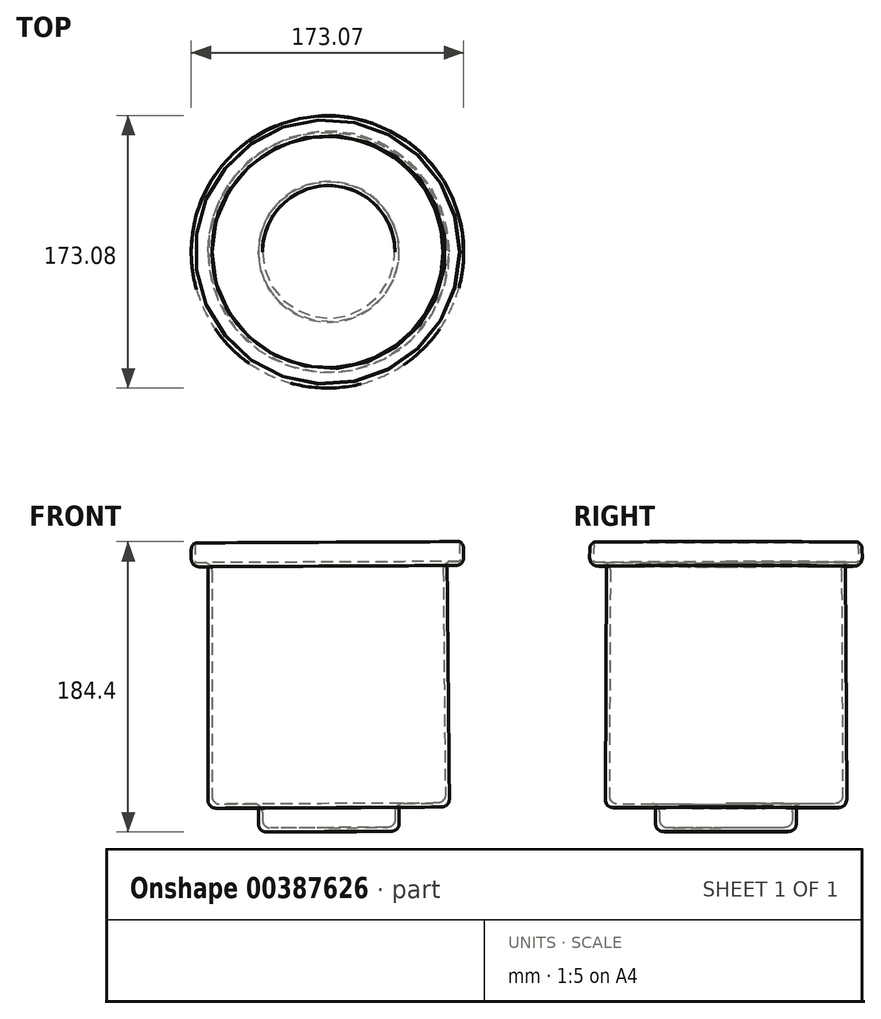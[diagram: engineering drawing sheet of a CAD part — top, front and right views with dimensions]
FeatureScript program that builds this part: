
annotation { "Feature Type Name" : "Feature", "Feature Type Description" : "" }
export const myFeature = defineFeature(function(context is Context, id is Id, definition is map)
    precondition{}
    {
        {
            var Q0;
            Q0=qCreatedBy(makeId("Front.planeOp"),FACE);
            var sketch = newSketch(context, id + "F0", { "sketchPlane" : qUnion([Q0])});
            skLineSegment(sketch, "E0.bottom", {"start": v(-75.88, 76.33) * mm, "end": v(76.77, 76.33) * mm});
            skLineSegment(sketch, "E0.top", {"start": v(-75.88, -77.03) * mm, "end": v(76.77, -77.03) * mm});
            skLineSegment(sketch, "E0.left", {"start": v(-75.88, 76.33) * mm, "end": v(-75.88, -77.03) * mm});
            skLineSegment(sketch, "E0.right", {"start": v(76.77, 76.33) * mm, "end": v(76.77, -77.03) * mm});
            skLineSegment(sketch, "E1.bottom", {"start": v(43.87, -77.03) * mm, "end": v(-43.87, -77.03) * mm});
            skLineSegment(sketch, "E1.top", {"start": v(43.87, -77.03) * mm, "end": v(-43.87, -77.03) * mm});
            skLineSegment(sketch, "E1.left", {"start": v(43.87, -77.03) * mm, "end": v(43.87, -77.03) * mm});
            skLineSegment(sketch, "E1.right", {"start": v(-43.87, -77.03) * mm, "end": v(-43.87, -77.03) * mm});
            skLineSegment(sketch, "E2.bottom", {"start": v(-43.87, -77.03) * mm, "end": v(43.87, -77.03) * mm});
            skLineSegment(sketch, "E2.top", {"start": v(-43.87, -92.1) * mm, "end": v(43.87, -92.1) * mm});
            skLineSegment(sketch, "E2.left", {"start": v(-43.87, -77.03) * mm, "end": v(-43.87, -92.1) * mm});
            skLineSegment(sketch, "E2.right", {"start": v(43.87, -77.03) * mm, "end": v(43.87, -92.1) * mm});
            skLineSegment(sketch, "E3.bottom", {"start": v(-86.49, 76.33) * mm, "end": v(88.27, 76.33) * mm});
            skLineSegment(sketch, "E3.top", {"start": v(-86.49, 91.48) * mm, "end": v(88.27, 91.48) * mm});
            skLineSegment(sketch, "E3.left", {"start": v(-86.49, 76.33) * mm, "end": v(-86.49, 91.48) * mm});
            skLineSegment(sketch, "E3.right", {"start": v(88.27, 76.33) * mm, "end": v(88.27, 91.48) * mm});
            skLineSegment(sketch, "E4", {"start": v(0, 91.48) * mm, "end": v(0.9, -92.1) * mm});
            skPoint(sketch, "E4.endSnap0", {"position": v(0.9, 91.48) * mm});
            skSolve(sketch);
        }
        {
            var Q0;
            {var subQ0=sQuery(id+"F0.wireOp",EDGE,"E2.left");Q0=makeQuery(id+"F0.imprint","IMPRINT",FACE,{"disambiguationData":[TD([[makeQuery(id+"F0.imprint","IMPRINT",EDGE,{"derivedFrom":subQ0}),1.0]])]});}
            var Q1;
            {var subQ1=sQuery(id+"F0.wireOp",EDGE,"E0.left");Q1=makeQuery(id+"F0.imprint","IMPRINT",FACE,{"disambiguationData":[TD([[makeQuery(id+"F0.imprint","IMPRINT",EDGE,{"derivedFrom":subQ1}),1.0]])]});}
            var Q2;
            {var subQ0=sQuery(id+"F0.wireOp",EDGE,"E3.left");Q2=makeQuery(id+"F0.imprint","IMPRINT",FACE,{"disambiguationData":[TD([[makeQuery(id+"F0.imprint","IMPRINT",EDGE,{"derivedFrom":subQ0}),-1.0]])]});}
            var Q3;
            Q3=sQuery(id+"F0.wireOp",EDGE,"E4");
            revolve(context, id + "F1", {"entities" : qUnion([Q0, Q1, Q2]), "axis" : qUnion([Q3]), "revolveType" : RevolveType.FULL, "oppositeDirection" : true});
        }
        {
            var Q0;
            Q0=makeQuery(id+"F1.opRevolve","SWEPT_FACE",FACE,{"disambiguationData":[OSD([sQuery(id+"F0.wireOp",EDGE,"E3.top")])]});
            shell(context, id + "F2", {"entities" : qUnion([Q0]), "thickness" : 2.54 * mm});
        }
        {
            var Q0;
            Q0=makeQuery(id+"F1.opRevolve","SWEPT_EDGE",EDGE,{"disambiguationData":[OSD([sQuery(id+"F0.wireOp",EDGE,"E3.top"),sQuery(id+"F0.wireOp",EDGE,"E3.left")])]});
            var Q1;
            Q1=makeQuery(id+"F1.opRevolve","SWEPT_EDGE",EDGE,{"disambiguationData":[OSD([sQuery(id+"F0.wireOp",EDGE,"E3.bottom"),sQuery(id+"F0.wireOp",EDGE,"E3.left")])]});
            fillet(context, id + "F3", {"entities" : qUnion([Q0, Q1]), "radius" : 5.08 * mm, "tangentPropagation" : true, "allowEdgeOverflow" : false});
        }
        {
            var Q0;
            Q0=makeQuery(id+"F1.opRevolve","SWEPT_EDGE",EDGE,{"disambiguationData":[OSD([sQuery(id+"F0.wireOp",EDGE,"E0.top"),sQuery(id+"F0.wireOp",EDGE,"E0.left")])]});
            var Q1;
            Q1=makeQuery(id+"F1.opRevolve","SWEPT_EDGE",EDGE,{"disambiguationData":[OSD([sQuery(id+"F0.wireOp",EDGE,"E2.top"),sQuery(id+"F0.wireOp",EDGE,"E2.left")])]});
            fillet(context, id + "F4", {"entities" : qUnion([Q0, Q1]), "radius" : 5.08 * mm, "tangentPropagation" : true, "allowEdgeOverflow" : false});
        }
        {
            var Q0;
            Q0=makeQuery(id+"F2.opShell","OFFSET_EDGE",EDGE,{"disambiguationData":[OSD([sQuery(id+"F0.wireOp",EDGE,"E0.left"),sQuery(id+"F0.wireOp",EDGE,"E3.bottom")])]});
            var Q1;
            Q1=makeQuery(id+"F2.opShell","OFFSET_EDGE",EDGE,{"disambiguationData":[OSD([sQuery(id+"F0.wireOp",EDGE,"E0.top"),sQuery(id+"F0.wireOp",EDGE,"E2.bottom"),sQuery(id+"F0.wireOp",EDGE,"E2.left")])]});
            fillet(context, id + "F5", {"entities" : qUnion([Q0, Q1]), "radius" : 5.08 * mm, "tangentPropagation" : true, "allowEdgeOverflow" : false});
        }
        {
            var Q0;
            Q0=makeQuery(id+"F2.opShell","OFFSET_FACE",FACE,{"disambiguationData":[OSD([sQuery(id+"F0.wireOp",EDGE,"E0.left")])]});
            fillet(context, id + "F6", {"entities" : qUnion([Q0]), "radius" : 5.08 * mm, "tangentPropagation" : true, "allowEdgeOverflow" : false});
        }
        {
            var Q0;
            Q0=makeQuery(id+"F2.opShell","OFFSET_FACE",FACE,{"disambiguationData":[OSD([sQuery(id+"F0.wireOp",EDGE,"E2.top")])]});
            fillet(context, id + "F7", {"entities" : qUnion([Q0]), "radius" : 5.08 * mm, "tangentPropagation" : true, "allowEdgeOverflow" : false});
        }
    });
